# Revit family: ГРЕЕРС ВС-1220
name_source: partatom
category: Wyposażenie mechaniczne
revit_build: Autodesk Revit 2016 (Build: 20150220_1215(x64)
units: mm (PartAtom-declared; Revit-internal decimal feet)

## family parameters
Obiekt nadrzędny = Powierzchnia
Punkt obliczania pomieszczeń = Nie
Tnij formami wycięć po wczytaniu = Nie
Typ części = Normalny
Współdzielony = Nie
Wymiar okrągłego złącza = Użyj średnicy

## types (1)
- ГРЕЕРС ВС-1220
    Domyślna rzędna = 2500 mm  [stored 8.2021 ft]
    IP = 54
    Model = ГРЕЕРС ВС-1220
    Opis = Водяной воздухонагреватель
    Producent = ГРЕЕРС
    Tемпература воды на выходе из теплообменника (Tw2) = 0 °C
    Автор = www.archispace.com
    Вентилятор = Осевой, однофазный, переменного тока с 3-скоростным вентилятором
    Вес аппарата = 0.00 kg
    Вес аппарата наполненного водой = 0.00 kg
    Данные продукта = https://greers.ru
    Классификация нагрузки = ДВИГАТЕЛЬ
    Количество воды проходящей через теплообменник = 0 L/s
    Коэффициент мощности = 1
    Макс. потребление тока = 0 A
    Материал = ГРЕЕРС-EPP-черный
    Напряжение питания = 230 V
    Падение давления воды в теплообменнике = 0 kPa
    Патрубки = 1/2"
    Полная мощность = 0 VA
    Производительность = 0 m³/h
    Температура воды на входе в теплообменник (Tw1) = 0 °C
    Температура воздуха на входе в аппарат (Тр1) = 0 °C
    Температура воздуха на выходе из аппарата (Тр2) = 0 °C
    Тепловая мощность = 0 kW

note: [stored X ft] marks values corroborated as IEEE doubles in the binary element streams (Revit-internal decimal feet)
